FCSTD DOCUMENT  (FreeCAD 1.0R)
Label: CWSensorKey-Assembly
License: All rights reserved
LicenseURL: https://en.wikipedia.org/wiki/All_rights_reserved
objects: App::Link×6, App::FeaturePython×5, Assembly::JointGroup×1, Assembly::AssemblyObject×1
EXTERNAL_REF file=../CW-Pad-Middle-Dit.FCStd obj=Body
EXTERNAL_REF file=../CW-Pad-Middle-Dah.FCStd obj=Body
EXTERNAL_REF file=../CW-Pad-Side.FCStd obj=Body
EXTERNAL_REF file=../CW-Pad-Holder.FCStd obj=Body

FEATURE [App::Link] CW_Pad_Middle_Dit  label="CW-Pad-Middle-Dit"
  LinkedObject = -> <external ../CW-Pad-Middle-Dit.FCStd>#Body
FEATURE [App::FeaturePython] GroundedJoint  # Assembly grounded joint (typed FeaturePython)
  ObjectToGround = -> CW_Pad_Middle_Dit
FEATURE [App::Link] CW_Pad_Middle_Dah  label="CW-Pad-Middle-Dah"
  LinkPlacement = pos=(3.1e-15,2,-2e-15) rot=(0,0,1;0rad)
  LinkedObject = -> <external ../CW-Pad-Middle-Dah.FCStd>#Body
  Placement = pos=(3.1e-15,2,-2e-15) rot=(0,0,1;0rad)
FEATURE [App::FeaturePython] Joint  label="Fixed"  # Assembly joint (typed FeaturePython)
  Activated = true
  AngleMax = 0
  AngleMin = 0
  Detach1 = false
  Detach2 = false
  Distance = 0
  Distance2 = 0
  EnableAngleMax = false
  EnableAngleMin = false
  EnableLengthMax = false
  EnableLengthMin = false
  JointType = 0 (Fixed)
  LengthMax = 0
  LengthMin = 0
  Placement1 = pos=(3.4,-1,7) rot=(0.707107,0,0.707107;3.14159rad)
  Placement2 = pos=(3.4,1,7) rot=(0.707107,0,0.707107;3.14159rad)
  Reference1 = -> Assembly [CW_Pad_Middle_Dah.Pad.Edge46,CW_Pad_Middle_Dah.Pad.Edge46]
  Reference2 = -> Assembly [CW_Pad_Middle_Dit.Pad.Edge45,CW_Pad_Middle_Dit.Pad.Edge45]
FEATURE [App::Link] CW_Pad_Side  label="CW-Pad-Side"
  LinkPlacement = pos=(3.1e-15,4,-1.6e-15) rot=(0,0,1;0rad)
  LinkedObject = -> <external ../CW-Pad-Side.FCStd>#Body
  Placement = pos=(3.1e-15,4,-1.6e-15) rot=(0,0,1;0rad)
FEATURE [App::Link] CW_Pad_Side001  label="CW-Pad-Side001"
  LinkPlacement = pos=(0,-2,0) rot=(0,0,1;0rad)
  LinkedObject = -> <external ../CW-Pad-Side.FCStd>#Body
  Placement = pos=(0,-2,0) rot=(0,0,1;0rad)
FEATURE [App::FeaturePython] Joint001  label="Fixed001"  # Assembly joint (typed FeaturePython)
  Activated = true
  AngleMax = 0
  AngleMin = 0
  Detach1 = false
  Detach2 = false
  Distance = 0
  Distance2 = 0
  EnableAngleMax = false
  EnableAngleMin = false
  EnableLengthMax = false
  EnableLengthMin = false
  JointType = 0 (Fixed)
  LengthMax = 0
  LengthMin = 0
  Placement1 = pos=(1.5,-1,12) rot=(0,0,1;0rad)
  Placement2 = pos=(1.5,1,12) rot=(0,0,1;0rad)
  Reference1 = -> Assembly [CW_Pad_Side.Pad.Vertex6,CW_Pad_Side.Pad.Vertex6]
  Reference2 = -> Assembly [CW_Pad_Middle_Dah.Pad.Vertex1,CW_Pad_Middle_Dah.Pad.Vertex1]
FEATURE [App::FeaturePython] Joint002  label="Fixed002"  # Assembly joint (typed FeaturePython)
  Activated = true
  AngleMax = 0
  AngleMin = 0
  Detach1 = false
  Detach2 = false
  Distance = 0
  Distance2 = 0
  EnableAngleMax = false
  EnableAngleMin = false
  EnableLengthMax = false
  EnableLengthMin = false
  JointType = 0 (Fixed)
  LengthMax = 0
  LengthMin = 0
  Placement1 = pos=(1.5,-1,12) rot=(0,0,1;0rad)
  Placement2 = pos=(1.5,1,12) rot=(0,0,1;0rad)
  Reference1 = -> Assembly [CW_Pad_Middle_Dit.Pad.Vertex2,CW_Pad_Middle_Dit.Pad.Vertex2]
  Reference2 = -> Assembly [CW_Pad_Side001.Pad.Vertex5,CW_Pad_Side001.Pad.Vertex5]
FEATURE [App::Link] Body
  LinkPlacement = pos=(3.85836,-1.3625,10.659) rot=(0.57735,0.57735,0.57735;2.0944rad)
  LinkedObject = -> <external ../CW-Pad-Holder.FCStd>#Body
  Placement = pos=(3.85836,-1.3625,10.659) rot=(0.57735,0.57735,0.57735;2.0944rad)
FEATURE [App::Link] Body001
  LinkPlacement = pos=(5.85836,-1.3625,10.659) rot=(0.57735,0.57735,0.57735;2.0944rad)
  LinkedObject = -> <external ../CW-Pad-Holder.FCStd>#Body
  Placement = pos=(5.85836,-1.3625,10.659) rot=(0.57735,0.57735,0.57735;2.0944rad)
FEATURE [App::FeaturePython] Joint003  label="Fixed003"  # Assembly joint (typed FeaturePython)
  Activated = true
  AngleMax = 0
  AngleMin = 0
  Detach1 = false
  Detach2 = false
  Distance = 0
  Distance2 = 0
  EnableAngleMax = false
  EnableAngleMin = false
  EnableLengthMax = false
  EnableLengthMin = false
  JointType = 0 (Fixed)
  LengthMax = 0
  LengthMin = 0
  Placement1 = pos=(-15,-1.8e-15,1) rot=(0,0,1;0rad)
  Placement2 = pos=(-15,0,-1) rot=(0,0,1;0rad)
  Reference1 = -> Assembly [Body.Pad.Edge51,Body.Pad.Edge51]
  Reference2 = -> Assembly [Body001.Pad.Edge50,Body001.Pad.Edge50]
FEATURE [Assembly::JointGroup] Joints
  Group = -> [GroundedJoint,Joint,Joint001,Joint002,Joint003]
FEATURE [Assembly::AssemblyObject] Assembly
  Group = -> [Joints,CW_Pad_Middle_Dit,GroundedJoint,CW_Pad_Middle_Dah,Joint,CW_Pad_Side,CW_Pad_Side001,Joint001,Joint002,Body,Body001,Joint003]
  Origin = -> Origin
  Type = Assembly

RESOLVED EXTERNAL PARTS (link-assembly join: the EXTERNAL_REF files above that resolve inside this repo's crawl, each included once):
---- part ../CW-Pad-Holder.FCStd = doc fcstd_470b1875ad9e ----
FCSTD DOCUMENT  (FreeCAD 1.0R)
Label: CW-Pad-Holder
License: All rights reserved
LicenseURL: https://en.wikipedia.org/wiki/All_rights_reserved
objects: Sketcher::SketchObject×1, PartDesign::Pad×1, PartDesign::Body×1, Part::Part2DObjectPython×1
note: 7 computed .brp shape members not serialized (recipe doc carries the construction recipe); baked Part::Feature solids carry a one-line shape summary decoded from their .brp

FEATURE [Sketcher::SketchObject] Sketch
  ArcFitTolerance = 1e-06
  FullyConstrained = true
  MakeInternals = false
  MapMode = 5
  sketch-geometry (23):
    g0: LineSegment StartX=21.5 StartY=-10 StartZ=0 EndX=21.5 EndY=12 EndZ=0
    g1: LineSegment StartX=21.5 StartY=12 StartZ=0 EndX=-21.5 EndY=12 EndZ=0
    g2: LineSegment StartX=-21.5 StartY=12 StartZ=0 EndX=-21.5 EndY=-10 EndZ=0
    g3: GeomPoint [constr] X=1e-16 Y=0 Z=0
    g4: LineSegment StartX=1.9 StartY=-10 StartZ=0 EndX=1.9 EndY=7 EndZ=0
    g5: LineSegment StartX=1.9 StartY=7 StartZ=0 EndX=-1.9 EndY=7 EndZ=0
    g6: LineSegment StartX=-1.9 StartY=7 StartZ=0 EndX=-1.9 EndY=-10 EndZ=0
    g7: GeomPoint [constr] X=0 Y=-1.5 Z=0
    g8: LineSegment [constr] StartX=15 StartY=12 StartZ=0 EndX=15 EndY=-10 EndZ=0
    g9: Circle CenterX=15 CenterY=0 CenterZ=0 NormalX=0 NormalY=0 NormalZ=1 AngleXU=0 Radius=1.55
    g10: Circle CenterX=-15 CenterY=0 CenterZ=0 NormalX=0 NormalY=0 NormalZ=1 AngleXU=0 Radius=1.55
    g11: LineSegment StartX=-12.25 StartY=-10 StartZ=0 EndX=-12.25 EndY=-6.5 EndZ=0
    g12: LineSegment StartX=-12.25 StartY=-6.5 StartZ=0 EndX=-15.75 EndY=-6.5 EndZ=0
    g13: LineSegment StartX=-15.75 StartY=-6.5 StartZ=0 EndX=-15.75 EndY=-10 EndZ=0
    g14: GeomPoint [constr] X=-14 Y=-8.25 Z=0
    g15: LineSegment StartX=-12.25 StartY=-10 StartZ=0 EndX=-1.9 EndY=-10 EndZ=0
    g16: LineSegment StartX=-21.5 StartY=-10 StartZ=0 EndX=-15.75 EndY=-10 EndZ=0
    g17: LineSegment StartX=15.75 StartY=-10 StartZ=0 EndX=15.75 EndY=-6.5 EndZ=0
    g18: LineSegment StartX=15.75 StartY=-6.5 StartZ=0 EndX=12.25 EndY=-6.5 EndZ=0
    g19: LineSegment StartX=12.25 StartY=-6.5 StartZ=0 EndX=12.25 EndY=-10 EndZ=0
    g20: GeomPoint [constr] X=14 Y=-8.25 Z=0
    g21: LineSegment StartX=15.75 StartY=-10 StartZ=0 EndX=21.5 EndY=-10 EndZ=0
    g22: LineSegment StartX=1.9 StartY=-10 StartZ=0 EndX=12.25 EndY=-10 EndZ=0
  constraints (60):
    c: Coincident(g21,g0)
    c: Coincident(g0,g1)
    c: Coincident(g1,g2)
    c: Coincident(g2,g16)
    c: Vertical(g0)
    c: Vertical(g2)
    c: Distance(g0,g2) = 43
    c: Distance(g16,g1) = 22
    c: Coincident(g3,g-1)
    c: Coincident(g4,g5)
    c: Coincident(g5,g6)
    c: Horizontal(g5)
    c: Vertical(g4)
    c: Vertical(g6)
    c: Symmetric(g5,g6,g7)
    c: Distance(g4,g6) = 3.8
    c: PointOnObject(g7,g-2)
    c: Horizontal(g4,g21)
    c: Coincident(g4,g22)
    c: Coincident(g6,g15)
    c: Horizontal(g4,g15)
    c: DistanceY(g5,g1) = 5
    c: DistanceY(g3,g0) = 12
    c: PointOnObject(g8,g1)
    c: Vertical(g8)
    c: Diameter(g9) = 3.1
    c: PointOnObject(g9,g8)
    c: PointOnObject(g9,g-1)
    c: Symmetric(g10,g9,g3)
    c: Equal(g10,g9)
    c: DistanceX(g3,g9) = 15
    c: Coincident(g11,g12)
    c: Coincident(g12,g13)
    c: Horizontal(g12)
    c: Vertical(g11)
    c: Vertical(g13)
    c: Symmetric(g12,g13,g14)
    c: Distance(g11,g13) = 3.5
    c: Distance(g13,g12) = 3.5
    c: Horizontal(g15)
    c: Horizontal(g16)
    c: Coincident(g16,g13)
    c: Coincident(g15,g11)
    c: Equal(g11,g13)
    c: Symmetric(g1,g0,g-2)
    c: Coincident(g17,g18)
    c: Coincident(g18,g19)
    c: Horizontal(g18)
    c: Vertical(g17)
    c: Vertical(g19)
    c: Symmetric(g18,g19,g20)
    c: Distance(g17,g19) = 3.5
    c: Distance(g19,g18) = 3.5
    c: PointOnObject(g8,g22)
    c: Coincident(g21,g17)
    c: Coincident(g19,g22)
    c: Parallel(g21,g1)
    c: Parallel(g22,g1)
    c: DistanceX(g14,g20) = 28
    c: Equal(g22,g15)
FEATURE [PartDesign::Pad] Pad
  Direction = (0,0,1)
  Length = 2
  Length2 = 10
  Midplane = true
  Profile = -> Sketch
  ReferenceAxis = -> Sketch [N_Axis]
  Refine = true
  Suppressed = false
  Type = 0
FEATURE [PartDesign::Body] Body
  AllowCompound = false
  Group = -> [Sketch,Pad]
  Origin = -> Origin
  Tip = -> Pad
FEATURE [Part::Part2DObjectPython] Shape2DView  # Draft 2D object (typed FeaturePython)
  AutoUpdate = true
  Base = -> Pad
  Clip = false
  FuseArch = false
  HiddenLines = false
  InPlace = true
  OnlySolids = false
  Projection = (0,0,1)
  ProjectionMode = 0
  SegmentLength = 0.05
  Tessellation = false
  VisibleOnly = false
---- part ../CW-Pad-Middle-Dah.FCStd = doc fcstd_d8498884f0ca ----
FCSTD DOCUMENT  (FreeCAD 1.0R)
Label: CW-Pad-Middle-Dah
License: All rights reserved
LicenseURL: https://en.wikipedia.org/wiki/All_rights_reserved
objects: Sketcher::SketchObject×1, PartDesign::Pad×1, PartDesign::Body×1, Part::Part2DObjectPython×1
note: 7 computed .brp shape members not serialized (recipe doc carries the construction recipe); baked Part::Feature solids carry a one-line shape summary decoded from their .brp

FEATURE [Sketcher::SketchObject] Sketch
  ArcFitTolerance = 1e-06
  AttachmentSupport = -> [XZ_Plane]
  FullyConstrained = true
  MakeInternals = false
  MapMode = 5
  Placement = pos=(0,0,0) rot=(1,0,0;1.5708rad)
  sketch-geometry (24):
    g0: GeomPoint [constr] X=0 Y=0 Z=0
    g1: GeomPoint [constr] X=0 Y=0 Z=0
    g2: LineSegment StartX=-15 StartY=-12 StartZ=0 EndX=4.5 EndY=-12 EndZ=0
    g3: LineSegment StartX=9 StartY=12 StartZ=0 EndX=5.3 EndY=12 EndZ=0
    g4: GeomPoint [constr] X=-3 Y=0 Z=0
    g5: ArcOfCircle CenterX=-15 CenterY=1e-16 CenterZ=0 NormalX=0 NormalY=0 NormalZ=1 AngleXU=0 Radius=12 StartAngle=1.5708 EndAngle=4.71239
    g6: LineSegment StartX=6.2 StartY=-12 StartZ=0 EndX=6.2 EndY=-10.45 EndZ=0
    g7: LineSegment StartX=6.2 StartY=-10.45 StartZ=0 EndX=4.5 EndY=-10.45 EndZ=0
    g8: LineSegment StartX=4.5 StartY=-10.45 StartZ=0 EndX=4.5 EndY=-12 EndZ=0
    g9: GeomPoint [constr] X=5.35 Y=-11.225 Z=0
    g10: LineSegment StartX=6.2 StartY=-12 StartZ=0 EndX=9 EndY=-12 EndZ=0
    g11: LineSegment StartX=1.5 StartY=7 StartZ=0 EndX=5.3 EndY=7 EndZ=0
    g12: LineSegment StartX=5.3 StartY=7 StartZ=0 EndX=5.3 EndY=12 EndZ=0
    g13: LineSegment StartX=1.5 StartY=12 StartZ=0 EndX=1.5 EndY=7 EndZ=0
    g14: GeomPoint [constr] X=3.4 Y=9.5 Z=0
    g15: LineSegment StartX=1.5 StartY=12 StartZ=0 EndX=-15 EndY=12 EndZ=0
    g16: Circle [constr] CenterX=-15 CenterY=1e-16 CenterZ=0 NormalX=0 NormalY=0 NormalZ=1 AngleXU=0 Radius=9.875
    g17: LineSegment [constr] StartX=1.5 StartY=30 StartZ=0 EndX=1.5 EndY=-30 EndZ=0
    g18: LineSegment StartX=-5.9714 StartY=-4 StartZ=0 EndX=9 EndY=-4 EndZ=0
    g19: LineSegment StartX=9 StartY=-2 StartZ=0 EndX=-5.9714 EndY=-2 EndZ=0
    g20: GeomPoint [constr] X=1.5143 Y=-3 Z=0
    g21: LineSegment StartX=9 StartY=-12 StartZ=0 EndX=9 EndY=-4 EndZ=0
    g22: LineSegment StartX=9 StartY=12 StartZ=0 EndX=9 EndY=-2 EndZ=0
    g23: ArcOfCircle CenterX=-7.70345 CenterY=-3 CenterZ=0 NormalX=0 NormalY=0 NormalZ=1 AngleXU=0 Radius=2 StartAngle=0.523599 EndAngle=5.75959
  constraints (61):
    c: Coincident(g0,g-1)
    c: Coincident(g1,g0)
    c: Horizontal(g2)
    c: Horizontal(g3)
    c: Symmetric(g3,g2,g4)
    c: Distance(g2,g15) = 24
    c: Horizontal(g4,g0)
    c: Coincident(g5,g2)
    c: Coincident(g5,g15)
    c: DistanceX(g5,g0) = 15
    c: Coincident(g6,g7)
    c: Coincident(g7,g8)
    c: Horizontal(g7)
    c: Vertical(g6)
    c: Vertical(g8)
    c: Symmetric(g7,g8,g9)
    c: DistanceX(g0,g8) = 4.5
    c: Equal(g8,g6)
    c: Parallel(g10,g2)
    c: Coincident(g6,g10)
    c: Coincident(g8,g2)
    c: Coincident(g11,g12)
    c: Coincident(g13,g11)
    c: Horizontal(g11)
    c: Vertical(g12)
    c: Vertical(g13)
    c: Symmetric(g12,g11,g14)
    c: DistanceX(g0,g13) = 1.5
    c: Coincident(g15,g13)
    c: Parallel(g15,g2)
    c: DistanceX(g13,g3) = 3.8
    c: Diameter(g16) = 19.75
    c: Coincident(g16,g5)
    c: DistanceY(g17,g17) = 60
    c: DistanceX(g0,g17) = 1.5
    c: Symmetric(g17,g17,g-1)
    c: DistanceY(g2,g7) = 1.55
    c: DistanceX(g2,g6) = 1.7
    c: Symmetric(g5,g2,g-1)
    c: DistanceX(g0,g3) = 9
    c: Coincident(g12,g3)
    c: DistanceY(g11,g3) = 5
    c: Vertical(g5,g5)
    c: Horizontal(g18)
    c: Horizontal(g19)
    c: Symmetric(g18,g19,g20)
    c: DistanceY(g-1,g20) = -3
    c: Vertical(g3,g19)
    c: Coincident(g21,g10)
    c: Coincident(g21,g18)
    c: Vertical(g21)
    c: Coincident(g22,g3)
    c: Coincident(g22,g19)
    c: Vertical(g3,g10)
    c: DistanceY(g18,g19) = 2
    c: Vertical(g19,g18)
    c: Horizontal(g23,g20)
    c: Diameter(g23) = 4
    c: Coincident(g23,g18)
    c: Vertical(g23,g19)
    c: PointOnObject(g18,g16)
FEATURE [PartDesign::Pad] Pad
  Direction = (0,-1,2e-16)
  Length = 2
  Length2 = 10
  Midplane = true
  Placement = pos=(0,0,0) rot=(1,0,0;1.5708rad)
  Profile = -> Sketch
  ReferenceAxis = -> Sketch [N_Axis]
  Refine = true
  Suppressed = false
  Type = 0
FEATURE [PartDesign::Body] Body  label="CW-Pad-Middle-Dah"
  AllowCompound = false
  Group = -> [Sketch,Pad]
  Origin = -> Origin
  Tip = -> Pad
FEATURE [Part::Part2DObjectPython] Shape2DView  # Draft 2D object (typed FeaturePython)
  AutoUpdate = true
  Base = -> Pad
  Clip = false
  FuseArch = false
  HiddenLines = false
  InPlace = true
  OnlySolids = false
  Projection = (0,-1,0)
  ProjectionMode = 0
  SegmentLength = 0.05
  Tessellation = false
  VisibleOnly = false
---- part ../CW-Pad-Middle-Dit.FCStd = doc fcstd_3442232d011e ----
FCSTD DOCUMENT  (FreeCAD 1.0R)
Label: CW-Pad-Middle-Dit
License: All rights reserved
LicenseURL: https://en.wikipedia.org/wiki/All_rights_reserved
objects: Sketcher::SketchObject×1, PartDesign::Pad×1, PartDesign::Body×1, Part::Part2DObjectPython×1
note: 7 computed .brp shape members not serialized (recipe doc carries the construction recipe); baked Part::Feature solids carry a one-line shape summary decoded from their .brp

FEATURE [Sketcher::SketchObject] Sketch
  ArcFitTolerance = 1e-06
  AttachmentSupport = -> [XZ_Plane]
  FullyConstrained = true
  MakeInternals = false
  MapMode = 5
  Placement = pos=(0,0,0) rot=(1,0,0;1.5708rad)
  sketch-geometry (24):
    g0: GeomPoint [constr] X=0 Y=0 Z=0
    g1: GeomPoint [constr] X=0 Y=0 Z=0
    g2: LineSegment StartX=-15 StartY=-12 StartZ=0 EndX=4.5 EndY=-12 EndZ=0
    g3: LineSegment StartX=9 StartY=12 StartZ=0 EndX=5.3 EndY=12 EndZ=0
    g4: GeomPoint [constr] X=-3 Y=0 Z=0
    g5: ArcOfCircle CenterX=-15 CenterY=4e-16 CenterZ=0 NormalX=0 NormalY=0 NormalZ=1 AngleXU=0 Radius=12 StartAngle=1.5708 EndAngle=4.71239
    g6: LineSegment StartX=6.2 StartY=-12 StartZ=0 EndX=6.2 EndY=-10.45 EndZ=0
    g7: LineSegment StartX=6.2 StartY=-10.45 StartZ=0 EndX=4.5 EndY=-10.45 EndZ=0
    g8: LineSegment StartX=4.5 StartY=-10.45 StartZ=0 EndX=4.5 EndY=-12 EndZ=0
    g9: GeomPoint [constr] X=5.35 Y=-11.225 Z=0
    g10: LineSegment StartX=6.2 StartY=-12 StartZ=0 EndX=9 EndY=-12 EndZ=0
    g11: LineSegment StartX=1.5 StartY=7 StartZ=0 EndX=5.3 EndY=7 EndZ=0
    g12: LineSegment StartX=5.3 StartY=7 StartZ=0 EndX=5.3 EndY=12 EndZ=0
    g13: LineSegment StartX=1.5 StartY=12 StartZ=0 EndX=1.5 EndY=7 EndZ=0
    g14: GeomPoint [constr] X=3.4 Y=9.5 Z=0
    g15: LineSegment StartX=1.5 StartY=12 StartZ=0 EndX=-15 EndY=12 EndZ=0
    g16: Circle [constr] CenterX=-15 CenterY=4e-16 CenterZ=0 NormalX=0 NormalY=0 NormalZ=1 AngleXU=0 Radius=9.875
    g17: LineSegment [constr] StartX=1.5 StartY=30 StartZ=0 EndX=1.5 EndY=-30 EndZ=0
    g18: LineSegment StartX=-5.9714 StartY=2 StartZ=0 EndX=9 EndY=2 EndZ=0
    g19: LineSegment StartX=9 StartY=4 StartZ=0 EndX=-5.9714 EndY=4 EndZ=0
    g20: GeomPoint [constr] X=1.5143 Y=3 Z=0
    g21: LineSegment StartX=9 StartY=-12 StartZ=0 EndX=9 EndY=2 EndZ=0
    g22: LineSegment StartX=9 StartY=12 StartZ=0 EndX=9 EndY=4 EndZ=0
    g23: ArcOfCircle CenterX=-7.70345 CenterY=3 CenterZ=0 NormalX=0 NormalY=0 NormalZ=1 AngleXU=0 Radius=2 StartAngle=0.523599 EndAngle=5.75959
  constraints (61):
    c: Coincident(g0,g-1)
    c: Coincident(g1,g0)
    c: Horizontal(g2)
    c: Horizontal(g3)
    c: Symmetric(g3,g2,g4)
    c: Distance(g2,g15) = 24
    c: Horizontal(g4,g0)
    c: Coincident(g5,g2)
    c: Coincident(g5,g15)
    c: DistanceX(g5,g0) = 15
    c: Coincident(g6,g7)
    c: Coincident(g7,g8)
    c: Horizontal(g7)
    c: Vertical(g6)
    c: Vertical(g8)
    c: Symmetric(g7,g8,g9)
    c: DistanceX(g0,g8) = 4.5
    c: Equal(g8,g6)
    c: Parallel(g10,g2)
    c: Coincident(g6,g10)
    c: Coincident(g8,g2)
    c: Coincident(g11,g12)
    c: Coincident(g13,g11)
    c: Horizontal(g11)
    c: Vertical(g12)
    c: Vertical(g13)
    c: Symmetric(g12,g11,g14)
    c: DistanceX(g0,g13) = 1.5
    c: Coincident(g15,g13)
    c: Parallel(g15,g2)
    c: DistanceX(g13,g3) = 3.8
    c: Diameter(g16) = 19.75
    c: Coincident(g16,g5)
    c: DistanceY(g17,g17) = 60
    c: DistanceX(g0,g17) = 1.5
    c: Symmetric(g17,g17,g-1)
    c: DistanceY(g2,g7) = 1.55
    c: DistanceX(g2,g6) = 1.7
    c: Symmetric(g5,g2,g-1)
    c: DistanceX(g0,g3) = 9
    c: Coincident(g12,g3)
    c: DistanceY(g11,g3) = 5
    c: Vertical(g5,g5)
    c: Horizontal(g18)
    c: Horizontal(g19)
    c: Symmetric(g18,g19,g20)
    c: DistanceY(g-1,g20) = 3
    c: Vertical(g3,g19)
    c: Coincident(g21,g10)
    c: Coincident(g21,g18)
    c: Vertical(g21)
    c: Coincident(g22,g3)
    c: Coincident(g22,g19)
    c: Vertical(g3,g10)
    c: DistanceY(g18,g19) = 2
    c: Vertical(g19,g18)
    c: Horizontal(g23,g20)
    c: Diameter(g23) = 4
    c: Coincident(g23,g18)
    c: Vertical(g23,g19)
    c: PointOnObject(g19,g16)
FEATURE [PartDesign::Pad] Pad
  Direction = (0,-1,2e-16)
  Length = 2
  Length2 = 10
  Midplane = true
  Placement = pos=(0,0,0) rot=(1,0,0;1.5708rad)
  Profile = -> Sketch
  ReferenceAxis = -> Sketch [N_Axis]
  Refine = true
  Suppressed = false
  Type = 0
FEATURE [PartDesign::Body] Body  label="CW-Pad-Middle-Dit"
  AllowCompound = false
  Group = -> [Sketch,Pad]
  Origin = -> Origin
  Tip = -> Pad
FEATURE [Part::Part2DObjectPython] Shape2DView  # Draft 2D object (typed FeaturePython)
  AutoUpdate = true
  Base = -> Pad
  Clip = false
  FuseArch = false
  HiddenLines = false
  InPlace = true
  OnlySolids = false
  Projection = (0,-1,0)
  ProjectionMode = 0
  SegmentLength = 0.05
  Tessellation = false
  VisibleOnly = false
---- part ../CW-Pad-Side.FCStd = doc fcstd_c18bf8d53188 ----
FCSTD DOCUMENT  (FreeCAD 1.0R)
Label: CW-Pad-Side
License: All rights reserved
LicenseURL: https://en.wikipedia.org/wiki/All_rights_reserved
objects: Sketcher::SketchObject×1, PartDesign::Pad×1, PartDesign::Body×1, Part::Part2DObjectPython×1
note: 7 computed .brp shape members not serialized (recipe doc carries the construction recipe); baked Part::Feature solids carry a one-line shape summary decoded from their .brp

FEATURE [Sketcher::SketchObject] Sketch
  ArcFitTolerance = 1e-06
  AttachmentSupport = -> [XZ_Plane]
  FullyConstrained = true
  MakeInternals = false
  MapMode = 5
  Placement = pos=(0,0,0) rot=(1,0,0;1.5708rad)
  sketch-geometry (9):
    g0: GeomPoint [constr] X=0 Y=0 Z=0
    g1: GeomPoint [constr] X=0 Y=0 Z=0
    g2: LineSegment StartX=-15 StartY=-12 StartZ=0 EndX=1.5 EndY=-12 EndZ=0
    g3: ArcOfCircle CenterX=-15 CenterY=8.3e-14 CenterZ=0 NormalX=0 NormalY=0 NormalZ=1 AngleXU=0 Radius=12 StartAngle=1.5708 EndAngle=4.71239
    g4: LineSegment StartX=1.5 StartY=12 StartZ=0 EndX=1.5 EndY=-12 EndZ=0
    g5: LineSegment StartX=1.5 StartY=12 StartZ=0 EndX=-15 EndY=12 EndZ=0
    g6: Circle [constr] CenterX=-15 CenterY=8.3e-14 CenterZ=0 NormalX=0 NormalY=0 NormalZ=1 AngleXU=0 Radius=9.875
    g7: LineSegment [constr] StartX=1.5 StartY=30 StartZ=0 EndX=1.5 EndY=-30 EndZ=0
    g8: Circle CenterX=-15 CenterY=8.3e-14 CenterZ=0 NormalX=0 NormalY=0 NormalZ=1 AngleXU=0 Radius=9.875
  constraints (21):
    c: Coincident(g0,g-1)
    c: Coincident(g1,g0)
    c: Horizontal(g2)
    c: Distance(g2,g5) = 24
    c: Coincident(g3,g2)
    c: Coincident(g3,g5)
    c: DistanceX(g3,g0) = 15
    c: Vertical(g4)
    c: DistanceX(g0,g4) = 1.5
    c: Coincident(g5,g4)
    c: Parallel(g5,g2)
    c: Diameter(g6) = 19.75
    c: Coincident(g6,g3)
    c: DistanceY(g7,g7) = 60
    c: DistanceX(g0,g7) = 1.5
    c: Symmetric(g7,g7,g-1)
    c: Symmetric(g3,g2,g-1)
    c: Vertical(g3,g3)
    c: Coincident(g2,g4)
    c: Diameter(g8) = 19.75
    c: Coincident(g8,g3)
FEATURE [PartDesign::Pad] Pad
  Direction = (0,-1,2e-16)
  Length = 2
  Length2 = 10
  Midplane = true
  Placement = pos=(0,0,0) rot=(1,0,0;1.5708rad)
  Profile = -> Sketch
  ReferenceAxis = -> Sketch [N_Axis]
  Refine = true
  Suppressed = false
  Type = 0
FEATURE [PartDesign::Body] Body  label="CW-Pad-Side"
  AllowCompound = false
  Group = -> [Sketch,Pad]
  Origin = -> Origin
  Tip = -> Pad
FEATURE [Part::Part2DObjectPython] Shape2DView  # Draft 2D object (typed FeaturePython)
  AutoUpdate = true
  Base = -> Pad
  Clip = false
  FuseArch = false
  HiddenLines = false
  InPlace = true
  OnlySolids = false
  Projection = (0,-1,0)
  ProjectionMode = 0
  SegmentLength = 0.05
  Tessellation = false
  VisibleOnly = false
